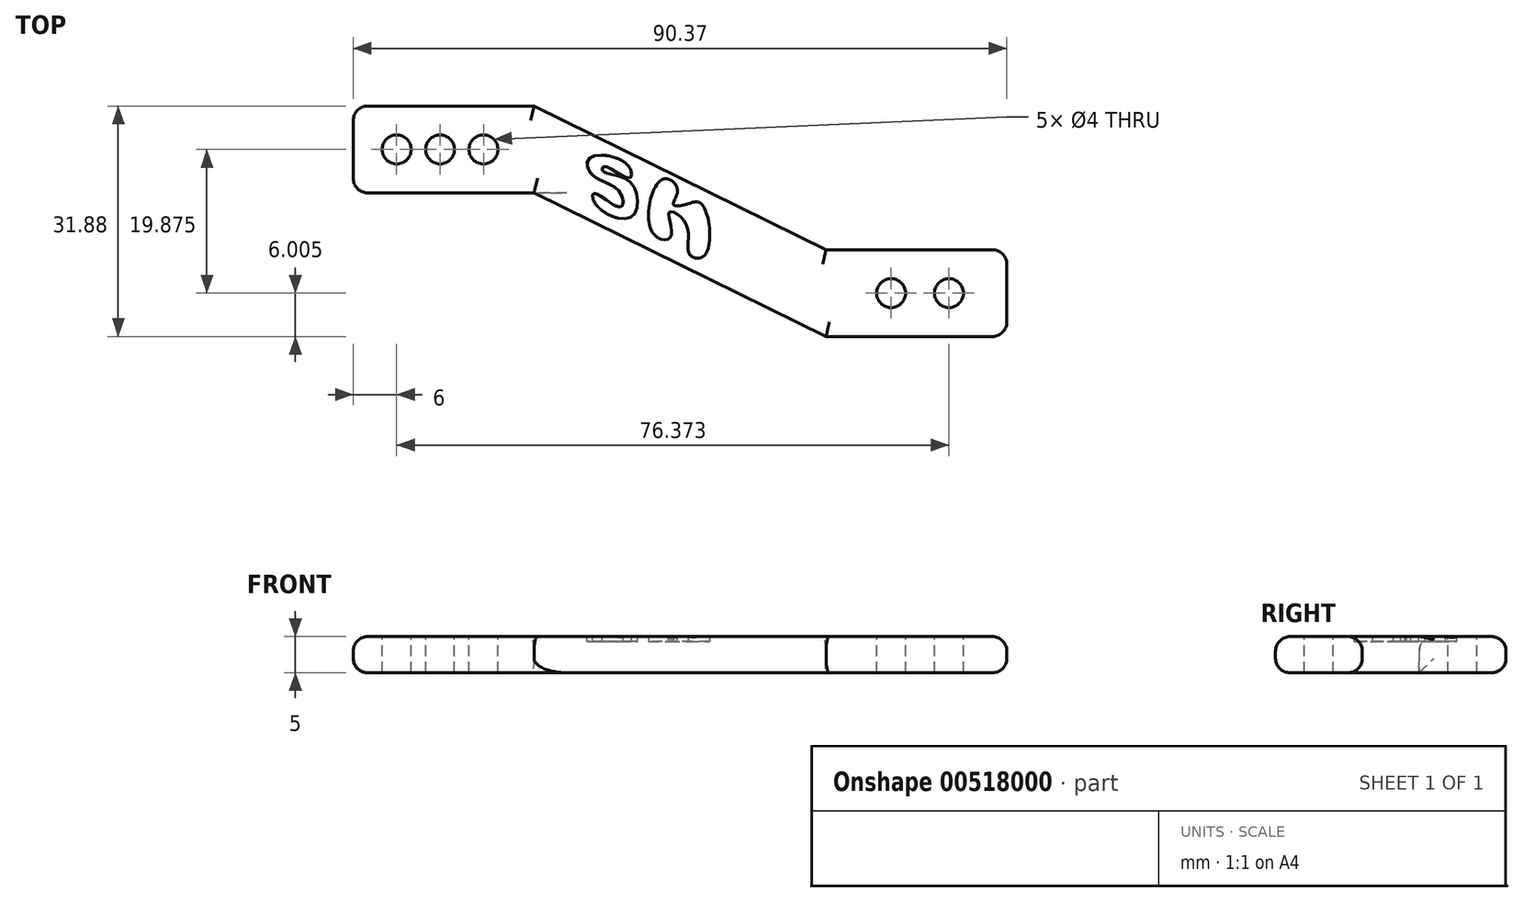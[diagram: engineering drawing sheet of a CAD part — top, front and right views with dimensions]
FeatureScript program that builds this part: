
annotation { "Feature Type Name" : "Feature", "Feature Type Description" : "" }
export const myFeature = defineFeature(function(context is Context, id is Id, definition is map)
    precondition{}
    {
        {
            var Q0;
            Q0=qCreatedBy(makeId("Top.planeOp"),FACE);
            var sketch = newSketch(context, id + "F0", { "sketchPlane" : qUnion([Q0])});
            skLineSegment(sketch, "E0.bottom", {"start": v(0, 0) * mm, "end": v(25, 0) * mm});
            skLineSegment(sketch, "E0.top", {"start": v(0, -12) * mm, "end": v(25, -12) * mm});
            skLineSegment(sketch, "E0.left", {"start": v(0, 0) * mm, "end": v(0, -12) * mm});
            skLineSegment(sketch, "E0.right", {"start": v(25, 0) * mm, "end": v(25, -12) * mm});
            skLineSegment(sketch, "E1", {"start": v(25, -12) * mm, "end": v(65.37, -31.88) * mm});
            skLineSegment(sketch, "E2", {"start": v(25, 0) * mm, "end": v(65.37, -19.88) * mm});
            skLineSegment(sketch, "E3", {"start": v(65.37, -19.88) * mm, "end": v(65.37, -31.88) * mm});
            skLineSegment(sketch, "E4.bottom", {"start": v(65.37, -19.88) * mm, "end": v(90.37, -19.88) * mm});
            skLineSegment(sketch, "E4.top", {"start": v(65.37, -31.88) * mm, "end": v(90.37, -31.88) * mm});
            skLineSegment(sketch, "E4.right", {"start": v(90.37, -19.88) * mm, "end": v(90.37, -31.88) * mm});
            skSolve(sketch);
        }
        {
            var Q0;
            Q0 = qSketchRegion(id + "F0", true);
            extrude(context, id + "F1", {"entities" : qUnion([Q0]), "depth" : 5 * mm, "offsetDistance" : 25 * mm});
        }
        {
            var Q0;
            Q0=makeQuery(id+"F1.opExtrude","CAP_FACE",FACE,{"disambiguationData":[OSD([sQuery(id+"F0.wireOp",EDGE,"E0.bottom"),sQuery(id+"F0.wireOp",EDGE,"E0.top"),sQuery(id+"F0.wireOp",EDGE,"E0.left"),sQuery(id+"F0.wireOp",EDGE,"E1"),sQuery(id+"F0.wireOp",EDGE,"E2"),sQuery(id+"F0.wireOp",EDGE,"E4.bottom"),sQuery(id+"F0.wireOp",EDGE,"E4.top"),sQuery(id+"F0.wireOp",EDGE,"E4.right")])],"isStart":false});
            var sketch = newSketch(context, id + "F2", { "sketchPlane" : qUnion([Q0])});
            skFitSpline(sketch, "E5", {"points": [v(33.56, -13.6) * mm, v(33.37, -12.08) * mm, v(36.94, -13.98) * mm, v(36.82, -11.83) * mm, v(33, -9.48) * mm, v(32.72, -7.18) * mm, v(37.9, -8.12) * mm, v(38.17, -9.95) * mm, v(34.7, -8.36) * mm, v(34.5, -8.98) * mm, v(38.35, -10.56) * mm, v(38.46, -15.32) * mm, v(33.56, -13.6) * mm]});
            skFitSpline(sketch, "E6", {"points": [v(42.76, -10.14) * mm, v(41.32, -17.39) * mm, v(43.91, -18.09) * mm, v(43.7, -14.72) * mm, v(46.1, -16.5) * mm, v(46.49, -20.47) * mm, v(48.66, -20.57) * mm, v(48.23, -13.6) * mm, v(45.98, -13.6) * mm, v(44.26, -13.6) * mm, v(44.83, -11.62) * mm, v(42.76, -10.14) * mm]});
            skSolve(sketch);
        }
        {
            var Q0;
            Q0=makeQuery(id+"F2.imprint","IMPRINT",FACE,{"disambiguationData":[TD([[makeQuery(id+"F2.imprint","IMPRINT",EDGE,{"derivedFrom":makeQuery(id+"F1.opExtrude","CAP_EDGE",EDGE,{"disambiguationData":[OSD([sQuery(id+"F0.wireOp",EDGE,"E0.bottom")])],"isStart":false})}),-1.0]])]});
            var sketch = newSketch(context, id + "F3", { "sketchPlane" : qUnion([Q0])});
            skCircle(sketch, "E7", {"center": v(6, -6) * mm, "radius": 2 * mm});
            skCircle(sketch, "E8", {"center": v(82.37, -25.88) * mm, "radius": 2 * mm});
            skCircle(sketch, "E9.1.0.0", {"center": v(74.37, -25.88) * mm, "radius": 2 * mm});
            skLineSegment(sketch, "E9.direction1", {"start": v(82.37, -25.88) * mm, "end": v(74.37, -25.88) * mm, "construction": true});
            skCircle(sketch, "E10.1.0.0", {"center": v(12, -6) * mm, "radius": 2 * mm});
            skCircle(sketch, "E10.2.0.0", {"center": v(18, -6) * mm, "radius": 2 * mm});
            skLineSegment(sketch, "E10.direction1", {"start": v(6, -6) * mm, "end": v(12, -6) * mm, "construction": true});
            skSolve(sketch);
        }
        {
            var Q0;
            Q0 = qSketchRegion(id + "F3", true);
            extrude(context, id + "F4", {"entities" : qUnion([Q0]), "operationType" : NewBodyOperationType.REMOVE, "endBound" : BoundingType.THROUGH_ALL, "oppositeDirection" : true, "depth" : 25 * mm, "offsetDistance" : 25 * mm});
        }
        {
            var Q0;
            Q0=makeQuery(id+"F1.opExtrude","CAP_EDGE",EDGE,{"disambiguationData":[OSD([sQuery(id+"F0.wireOp",EDGE,"E4.right")])],"isStart":false});
            var Q1;
            Q1=makeQuery(id+"F1.opExtrude","CAP_EDGE",EDGE,{"disambiguationData":[OSD([sQuery(id+"F0.wireOp",EDGE,"E0.left")])],"isStart":false});
            fillet(context, id + "F5", {"entities" : qUnion([Q0, Q1]), "radius" : 2 * mm, "tangentPropagation" : true, "allowEdgeOverflow" : false});
        }
        {
            var Q0;
            Q0=makeQuery(id+"F1.opExtrude","CAP_EDGE",EDGE,{"disambiguationData":[OSD([sQuery(id+"F0.wireOp",EDGE,"E0.bottom")])],"isStart":false});
            var Q1;
            Q1=makeQuery(id+"F1.opExtrude","CAP_EDGE",EDGE,{"disambiguationData":[OSD([sQuery(id+"F0.wireOp",EDGE,"E2")])],"isStart":false});
            var Q2;
            Q2=makeQuery(id+"F1.opExtrude","CAP_EDGE",EDGE,{"disambiguationData":[OSD([sQuery(id+"F0.wireOp",EDGE,"E4.bottom")])],"isStart":false});
            var Q3;
            {var subQ0=sQuery(id+"F0.wireOp",EDGE,"E4.right");Q3=makeQuery(id+"F5.opFillet","BLEND_EDGE",EDGE,{"blendedFrom":[makeQuery(id+"F1.opExtrude","CAP_EDGE",EDGE,{"disambiguationData":[OSD([subQ0])],"isStart":false}),makeQuery(id+"F1.opExtrude","CAP_FACE",FACE,{"disambiguationData":[OSD([sQuery(id+"F0.wireOp",EDGE,"E0.bottom"),sQuery(id+"F0.wireOp",EDGE,"E0.top"),sQuery(id+"F0.wireOp",EDGE,"E0.left"),sQuery(id+"F0.wireOp",EDGE,"E1"),sQuery(id+"F0.wireOp",EDGE,"E2"),sQuery(id+"F0.wireOp",EDGE,"E4.bottom"),sQuery(id+"F0.wireOp",EDGE,"E4.top"),subQ0])],"isStart":false})],"blendedInto":[makeQuery(id+"F1.opExtrude","CAP_FACE",FACE,{"disambiguationData":[OSD([sQuery(id+"F0.wireOp",EDGE,"E0.bottom"),sQuery(id+"F0.wireOp",EDGE,"E0.top"),sQuery(id+"F0.wireOp",EDGE,"E0.left"),sQuery(id+"F0.wireOp",EDGE,"E1"),sQuery(id+"F0.wireOp",EDGE,"E2"),sQuery(id+"F0.wireOp",EDGE,"E4.bottom"),sQuery(id+"F0.wireOp",EDGE,"E4.top"),subQ0])],"isStart":false})]});}
            var Q4;
            Q4=makeQuery(id+"F1.opExtrude","CAP_EDGE",EDGE,{"disambiguationData":[OSD([sQuery(id+"F0.wireOp",EDGE,"E4.top")])],"isStart":false});
            var Q5;
            Q5=makeQuery(id+"F1.opExtrude","CAP_EDGE",EDGE,{"disambiguationData":[OSD([sQuery(id+"F0.wireOp",EDGE,"E1")])],"isStart":false});
            var Q6;
            Q6=makeQuery(id+"F1.opExtrude","CAP_EDGE",EDGE,{"disambiguationData":[OSD([sQuery(id+"F0.wireOp",EDGE,"E0.top")])],"isStart":false});
            var Q7;
            {var subQ0=sQuery(id+"F0.wireOp",EDGE,"E0.left");Q7=makeQuery(id+"F5.opFillet","BLEND_EDGE",EDGE,{"blendedFrom":[makeQuery(id+"F1.opExtrude","CAP_EDGE",EDGE,{"disambiguationData":[OSD([subQ0])],"isStart":false}),makeQuery(id+"F1.opExtrude","CAP_FACE",FACE,{"disambiguationData":[OSD([sQuery(id+"F0.wireOp",EDGE,"E0.bottom"),sQuery(id+"F0.wireOp",EDGE,"E0.top"),subQ0,sQuery(id+"F0.wireOp",EDGE,"E1"),sQuery(id+"F0.wireOp",EDGE,"E2"),sQuery(id+"F0.wireOp",EDGE,"E4.bottom"),sQuery(id+"F0.wireOp",EDGE,"E4.top"),sQuery(id+"F0.wireOp",EDGE,"E4.right")])],"isStart":false})],"blendedInto":[makeQuery(id+"F1.opExtrude","CAP_FACE",FACE,{"disambiguationData":[OSD([sQuery(id+"F0.wireOp",EDGE,"E0.bottom"),sQuery(id+"F0.wireOp",EDGE,"E0.top"),subQ0,sQuery(id+"F0.wireOp",EDGE,"E1"),sQuery(id+"F0.wireOp",EDGE,"E2"),sQuery(id+"F0.wireOp",EDGE,"E4.bottom"),sQuery(id+"F0.wireOp",EDGE,"E4.top"),sQuery(id+"F0.wireOp",EDGE,"E4.right")])],"isStart":false})]});}
            var Q8;
            Q8=makeQuery(id+"F1.opExtrude","CAP_EDGE",EDGE,{"disambiguationData":[OSD([sQuery(id+"F0.wireOp",EDGE,"E1")])],"isStart":true});
            var Q9;
            Q9=makeQuery(id+"F1.opExtrude","CAP_EDGE",EDGE,{"disambiguationData":[OSD([sQuery(id+"F0.wireOp",EDGE,"E4.top")])],"isStart":true});
            var Q10;
            Q10=makeQuery(id+"F1.opExtrude","CAP_EDGE",EDGE,{"disambiguationData":[OSD([sQuery(id+"F0.wireOp",EDGE,"E4.right")])],"isStart":true});
            var Q11;
            Q11=makeQuery(id+"F1.opExtrude","CAP_EDGE",EDGE,{"disambiguationData":[OSD([sQuery(id+"F0.wireOp",EDGE,"E4.bottom")])],"isStart":true});
            var Q12;
            Q12=makeQuery(id+"F1.opExtrude","CAP_EDGE",EDGE,{"disambiguationData":[OSD([sQuery(id+"F0.wireOp",EDGE,"E2")])],"isStart":true});
            var Q13;
            Q13=makeQuery(id+"F1.opExtrude","CAP_EDGE",EDGE,{"disambiguationData":[OSD([sQuery(id+"F0.wireOp",EDGE,"E0.bottom")])],"isStart":true});
            var Q14;
            Q14=makeQuery(id+"F1.opExtrude","CAP_EDGE",EDGE,{"disambiguationData":[OSD([sQuery(id+"F0.wireOp",EDGE,"E0.left")])],"isStart":true});
            fillet(context, id + "F6", {"entities" : qUnion([Q0, Q1, Q2, Q3, Q4, Q5, Q6, Q7, Q8, Q9, Q10, Q11, Q12, Q13, Q14]), "radius" : 2 * mm, "tangentPropagation" : true, "allowEdgeOverflow" : false});
        }
        {
            var Q0;
            Q0 = qSketchRegion(id + "F2", true);
            extrude(context, id + "F7", {"entities" : qUnion([Q0]), "operationType" : NewBodyOperationType.REMOVE, "oppositeDirection" : true, "depth" : .7 * mm, "offsetDistance" : 25 * mm});
        }
    });
